# Revit family: Aluco Fire SL 2P (HI) (pl)
name_source: partatom
category: Modele ogólne
units: mm (PartAtom-declared; Revit-internal decimal feet)

## family parameters
Może być obiektem nadrzędnym dla zbrojenia = Nie
Numer OmniClass = 23.60.70.14.11
Oparty na płaszczyźnie roboczej = Tak
Punkt obliczania pomieszczeń = Nie
Tnij formami wycięć po wczytaniu = Tak
Typ części = Normalny
Tytuł OmniClass = Smoke Dampers
Współdzielony = Nie
Wymiar okrągłego złącza = Użyj średnicy
Zawsze pionowo = Nie

## types (6) — shared parameters
IfcExportAs = "IfcWindowType"
Klasa bezpieczeństwa pożarowego = BRoof (t1)
Klasa bezpieczeństwa przed upadkiem z wysokości = SB 1200
Klasa odporności na działanie wysokiej temperatury = B 300
Klasyfikacja na działanie wiatru = WL 1500
Kąt otwarcia = 90.00°
Maksymalne obciążenie śniegiem = SL 1500
Materiał owiewki = Aluco - stal ocynkowana
Materiał profili = Aluco - aluminium
Materiał płyt = Aluco - poliwęglan
Obraz typu = ALUCO FIRE SL 1P (HI).png
Opis = Klapa oddymiająca dwuskrzydłowa w pasmach łukowych
Pewność działania = RE 10000
Potwierdzone działanie w skrajnie niskich temperaturach = T -15
Producent = ALUCO SYSTEM SP. Z O.O
URL = https://aluco.com.pl
URL produktu = https://aluco.com.pl
zero-valued in all types: Domyślna rzędna

## per-type parameters (varying)
| type | Komentarze do typu | Model | Rodzaj napędu | System bezmostkowy | System ekonomiczny | Zasilanie |
| system ekonomiczny z napędem pneumatycznym | Klapa oddymiająca w systemie ekonomicznym | FIRE SL 2P | napęd pneumatyczny | Nie | Tak | 0 V |
| system bezmostkowy z napędem pneumatycznym | Klapa oddymiająca w systemie bezmostkowym o podwyższonej izolacyjności termicznej | FIRE SL 2P (HI) | napęd pneumatyczny | Tak | Nie | 0 V |
| system bezmostkowy z napędem elektrycznym | Klapa oddymiająca w systemie bezmostkowym o podwyższonej izolacyjności termicznej | FIRE SL 2P (HI) | napęd elektryczny | Tak | Nie | 230 V |
| system ekonomiczny z napędem elektrycznym | Klapa oddymiająca w systemie ekonomicznym | FIRE SL 2P (HI) | napęd elektryczny | Tak | Nie | 230 V |
| system ekonomiczny z napędem pneumatyczno-elektrycznym | Klapa oddymiająca w systemie ekonomicznym | FIRE SL 2P (HI) | napęd pneumatyczno-elektryczny | Tak | Nie | 230 V |
| system bezmostkowy z napędem pneumatyczno-elektrycznym | Klapa oddymiająca w systemie bezmostkowym o podwyższonej izolacyjności termicznej | FIRE SL 2P (HI) | napęd pneumatyczno-elektryczny | Tak | Nie | 230 V |
